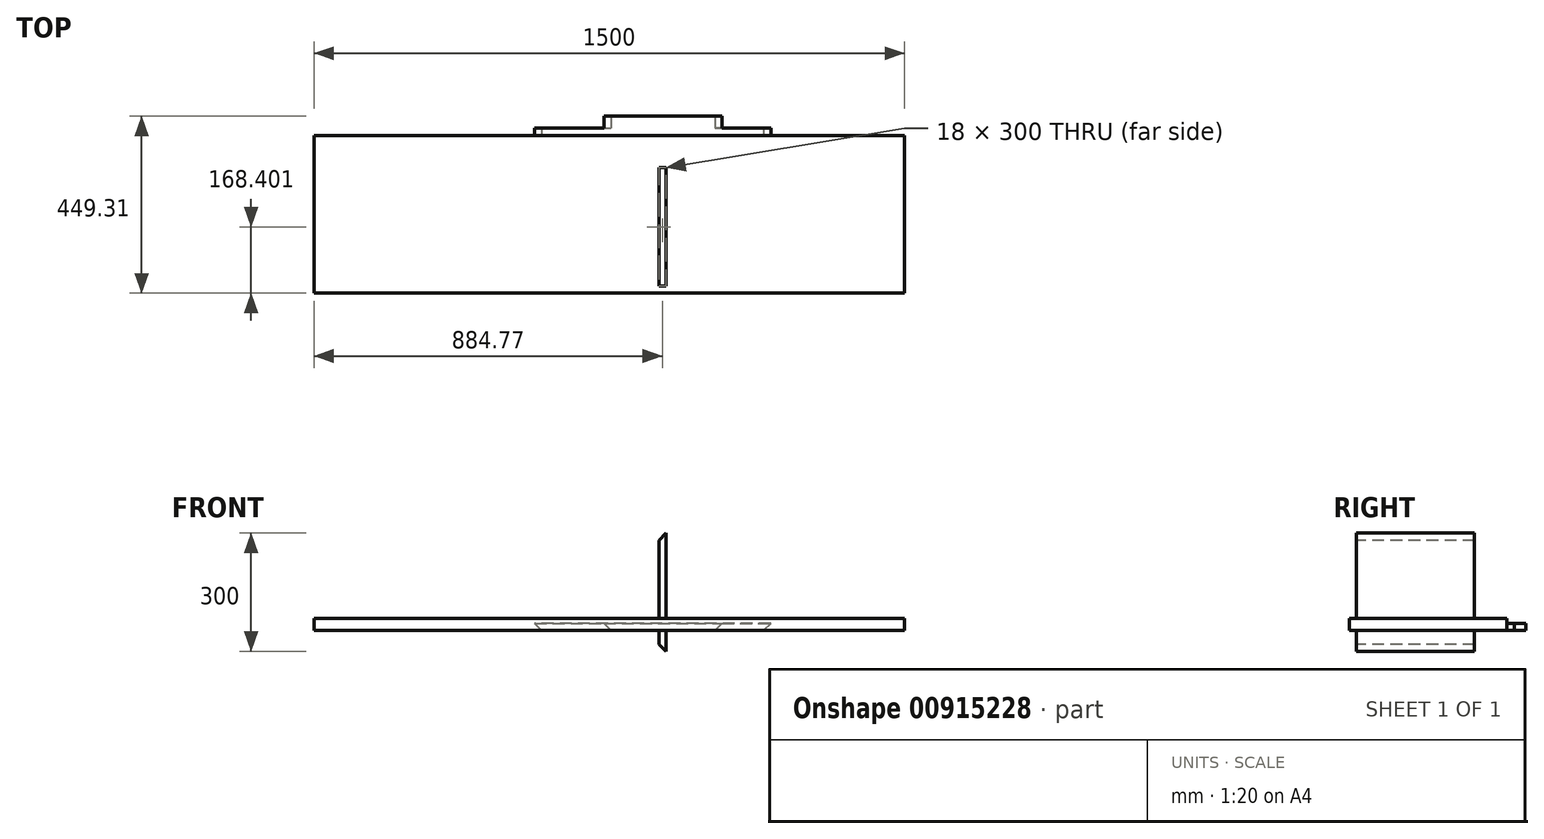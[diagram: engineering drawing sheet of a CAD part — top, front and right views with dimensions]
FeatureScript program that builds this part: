
annotation { "Feature Type Name" : "Feature", "Feature Type Description" : "" }
export const myFeature = defineFeature(function(context is Context, id is Id, definition is map)
    precondition{}
    {
        {
            var Q0;
            Q0=qCreatedBy(makeId("Top.planeOp"),FACE);
            var sketch = newSketch(context, id + "F0", { "sketchPlane" : qUnion([Q0])});
            skLineSegment(sketch, "E0.bottom", {"start": v(-139.75, 177.27) * mm, "end": v(160.25, 177.27) * mm});
            skLineSegment(sketch, "E0.top", {"start": v(-139.75, -122.73) * mm, "end": v(160.25, -122.73) * mm});
            skLineSegment(sketch, "E0.left", {"start": v(-139.75, 177.27) * mm, "end": v(-139.75, -122.73) * mm});
            skLineSegment(sketch, "E0.right", {"start": v(160.25, 177.27) * mm, "end": v(160.25, -122.73) * mm});
            skSolve(sketch);
        }
        {
            var Q0;
            Q0 = qSketchRegion(id + "F0", true);
            extrude(context, id + "F1", {"entities" : qUnion([Q0]), "depth" : 18 * mm, "offsetDistance" : 25 * mm});
        }
        {
            var Q0;
            Q0=makeQuery(id+"F1.opExtrude","SWEPT_FACE",FACE,{"disambiguationData":[OSD([sQuery(id+"F0.wireOp",EDGE,"E0.top")])]});
            var sketch = newSketch(context, id + "F2", { "sketchPlane" : qUnion([Q0])});
            skLineSegment(sketch, "E1", {"start": v(-139.75, 18) * mm, "end": v(-121.75, 0) * mm});
            skLineSegment(sketch, "E2", {"start": v(-121.75, 0) * mm, "end": v(-139.75, 0) * mm});
            skLineSegment(sketch, "E3", {"start": v(-139.75, 0) * mm, "end": v(-139.75, 18) * mm});
            skLineSegment(sketch, "E4", {"start": v(160.25, 18) * mm, "end": v(142.25, 0) * mm});
            skLineSegment(sketch, "E5", {"start": v(142.25, 0) * mm, "end": v(160.25, 0) * mm});
            skLineSegment(sketch, "E6", {"start": v(160.25, 0) * mm, "end": v(160.25, 18) * mm});
            skSolve(sketch);
        }
        {
            var Q0;
            Q0 = qSketchRegion(id + "F2", true);
            extrude(context, id + "F3", {"entities" : qUnion([Q0]), "operationType" : NewBodyOperationType.REMOVE, "oppositeDirection" : true, "depth" : 500 * mm, "offsetDistance" : 25 * mm});
        }
        {
            var Q0;
            Q0=qCreatedBy(makeId("Right.planeOp"),FACE);
            var sketch = newSketch(context, id + "F4", { "sketchPlane" : qUnion([Q0])});
            skLineSegment(sketch, "E7.bottom", {"start": v(-253.64, 246.93) * mm, "end": v(46.36, 246.93) * mm});
            skLineSegment(sketch, "E7.top", {"start": v(-253.64, -53.07) * mm, "end": v(46.36, -53.07) * mm});
            skLineSegment(sketch, "E7.left", {"start": v(-253.64, 246.93) * mm, "end": v(-253.64, -53.07) * mm});
            skLineSegment(sketch, "E7.right", {"start": v(46.36, 246.93) * mm, "end": v(46.36, -53.07) * mm});
            skSolve(sketch);
        }
        {
            var Q0;
            Q0 = qSketchRegion(id + "F4", true);
            extrude(context, id + "F5", {"entities" : qUnion([Q0]), "depth" : 18 * mm, "offsetDistance" : 25 * mm});
        }
        {
            var Q0;
            Q0=makeQuery(id+"F5.opExtrude","SWEPT_FACE",FACE,{"disambiguationData":[OSD([sQuery(id+"F4.wireOp",EDGE,"E7.left")])]});
            var sketch = newSketch(context, id + "F6", { "sketchPlane" : qUnion([Q0])});
            skLineSegment(sketch, "E8", {"start": v(18, 246.93) * mm, "end": v(0, 228.93) * mm});
            skLineSegment(sketch, "E9", {"start": v(0, 228.93) * mm, "end": v(0, 246.93) * mm});
            skLineSegment(sketch, "E10", {"start": v(0, 246.93) * mm, "end": v(18, 246.93) * mm});
            skLineSegment(sketch, "E11", {"start": v(18, -53.07) * mm, "end": v(0, -35.07) * mm});
            skLineSegment(sketch, "E12", {"start": v(0, -35.07) * mm, "end": v(0, -53.07) * mm});
            skLineSegment(sketch, "E13", {"start": v(0, -53.07) * mm, "end": v(18, -53.07) * mm});
            skSolve(sketch);
        }
        {
            var Q0;
            Q0 = qSketchRegion(id + "F6", true);
            extrude(context, id + "F7", {"entities" : qUnion([Q0]), "operationType" : NewBodyOperationType.REMOVE, "oppositeDirection" : true, "depth" : 500 * mm, "offsetDistance" : 25 * mm});
        }
        {
            var Q0;
            Q0=qCreatedBy(makeId("Top.planeOp"),FACE);
            var sketch = newSketch(context, id + "F8", { "sketchPlane" : qUnion([Q0])});
            skLineSegment(sketch, "E14.bottom", {"start": v(-315.6, 147.27) * mm, "end": v(284.4, 147.27) * mm});
            skLineSegment(sketch, "E14.top", {"start": v(-315.6, -152.73) * mm, "end": v(284.4, -152.73) * mm});
            skLineSegment(sketch, "E14.left", {"start": v(-315.6, 147.27) * mm, "end": v(-315.6, -152.73) * mm});
            skLineSegment(sketch, "E14.right", {"start": v(284.4, 147.27) * mm, "end": v(284.4, -152.73) * mm});
            skSolve(sketch);
        }
        {
            var Q0;
            Q0 = qSketchRegion(id + "F8", true);
            extrude(context, id + "F9", {"entities" : qUnion([Q0]), "depth" : 18 * mm, "offsetDistance" : 25 * mm});
        }
        {
            var Q0;
            Q0=makeQuery(id+"F9.opExtrude","SWEPT_FACE",FACE,{"disambiguationData":[OSD([sQuery(id+"F8.wireOp",EDGE,"E14.top")])]});
            var sketch = newSketch(context, id + "F10", { "sketchPlane" : qUnion([Q0])});
            skLineSegment(sketch, "E15", {"start": v(-315.6, 18) * mm, "end": v(-297.6, 0) * mm});
            skLineSegment(sketch, "E16", {"start": v(-297.6, 0) * mm, "end": v(-315.6, 0) * mm});
            skLineSegment(sketch, "E17", {"start": v(-315.6, 0) * mm, "end": v(-315.6, 18) * mm});
            skLineSegment(sketch, "E18", {"start": v(284.4, 18) * mm, "end": v(266.4, 0) * mm});
            skLineSegment(sketch, "E19", {"start": v(266.4, 0) * mm, "end": v(284.4, 0) * mm});
            skLineSegment(sketch, "E20", {"start": v(284.4, 0) * mm, "end": v(284.4, 18) * mm});
            skSolve(sketch);
        }
        {
            var Q0;
            Q0 = qSketchRegion(id + "F10", true);
            extrude(context, id + "F11", {"entities" : qUnion([Q0]), "operationType" : NewBodyOperationType.REMOVE, "oppositeDirection" : true, "depth" : 500 * mm, "offsetDistance" : 25 * mm});
        }
        {
            var Q0;
            Q0=qCreatedBy(makeId("Top.planeOp"),FACE);
            var sketch = newSketch(context, id + "F12", { "sketchPlane" : qUnion([Q0])});
            skLineSegment(sketch, "E21.bottom", {"start": v(-875.77, 127.96) * mm, "end": v(624.23, 127.96) * mm});
            skLineSegment(sketch, "E21.top", {"start": v(-875.77, -272.04) * mm, "end": v(624.23, -272.04) * mm});
            skLineSegment(sketch, "E21.left", {"start": v(-875.77, 127.96) * mm, "end": v(-875.77, -272.04) * mm});
            skLineSegment(sketch, "E21.right", {"start": v(624.23, 127.96) * mm, "end": v(624.23, -272.04) * mm});
            skSolve(sketch);
        }
        {
            var Q0;
            Q0 = qSketchRegion(id + "F12", true);
            extrude(context, id + "F13", {"entities" : qUnion([Q0]), "depth" : 30 * mm, "offsetDistance" : 25 * mm});
        }
        {
            var Q0;
            Q0 = qSketchRegion(id + "F12", true);
            extrude(context, id + "F14", {"entities" : qUnion([Q0]), "operationType" : NewBodyOperationType.ADD, "depth" : 30 * mm, "offsetDistance" : 25 * mm});
        }
        {
            var Q0;
            Q0=qCreatedBy(makeId("Right.planeOp"),FACE);
            var sketch = newSketch(context, id + "F15", { "sketchPlane" : qUnion([Q0])});
            skLineSegment(sketch, "E22.bottom", {"start": v(-229.3, 1300.8) * mm, "end": v(170.7, 1300.8) * mm});
            skLineSegment(sketch, "E22.top", {"start": v(-229.3, -799.2) * mm, "end": v(170.7, -799.2) * mm});
            skLineSegment(sketch, "E22.left", {"start": v(-229.3, 1300.8) * mm, "end": v(-229.3, -799.2) * mm});
            skLineSegment(sketch, "E22.right", {"start": v(170.7, 1300.8) * mm, "end": v(170.7, -799.2) * mm});
            skSolve(sketch);
        }
        {
            var Q0;
            Q0 = qSketchRegion(id + "F15", true);
            extrude(context, id + "F16", {"entities" : qUnion([Q0]), "depth" : 30 * mm, "offsetDistance" : 25 * mm});
        }
        {
            var Q0;
            Q0=makeQuery(id+"F13.opExtrude","SWEPT_BODY",BODY,{"disambiguationData":[OSD([sQuery(id+"F12.wireOp",EDGE,"E21.bottom"),sQuery(id+"F12.wireOp",EDGE,"E21.top"),sQuery(id+"F12.wireOp",EDGE,"E21.left"),sQuery(id+"F12.wireOp",EDGE,"E21.right")])]});
            var Q1;
            Q1=makeQuery(id+"F16.opExtrude","SWEPT_BODY",BODY,{"disambiguationData":[OSD([sQuery(id+"F15.wireOp",EDGE,"E22.bottom"),sQuery(id+"F15.wireOp",EDGE,"E22.top"),sQuery(id+"F15.wireOp",EDGE,"E22.left"),sQuery(id+"F15.wireOp",EDGE,"E22.right")])]});
            deleteBodies(context, id + "F17", {"entities" : qUnion([Q0, Q1])});
        }
    });
